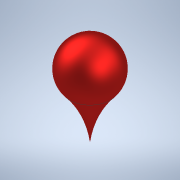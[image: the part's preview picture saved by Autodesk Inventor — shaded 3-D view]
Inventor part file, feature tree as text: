
AUTODESK INVENTOR PART (.ipt)
format: ipt  version: 2021 (Build 250183000, 183)  size: 169,472 bytes
history: native  units: in
note: dims shown in document units (in); Inventor stores cm internally (conversion verified against a paired STEP export)
features: revolve x2, sketch x2
ambient origin geometry x8: Origin, YZ Plane, XZ Plane, XY Plane, X Axis, Y Axis, Z Axis, Center Point
bodies: Solid1 (feature_tree)
feature tree (4):
  revolve  "Revolution1"  [1 undecoded]
  revolve  "Revolution2"  [1 undecoded]
  sketch  "Sketch1"  dims[d0=1.0in d1=0.0in]
  sketch  "Sketch2"  dims[d2=90.0deg]
note: 2 required parameter values undecoded (feature->parameter linkage not recoverable at this tier; creation-order binding heuristic only, values carry confidence <= 0.55)